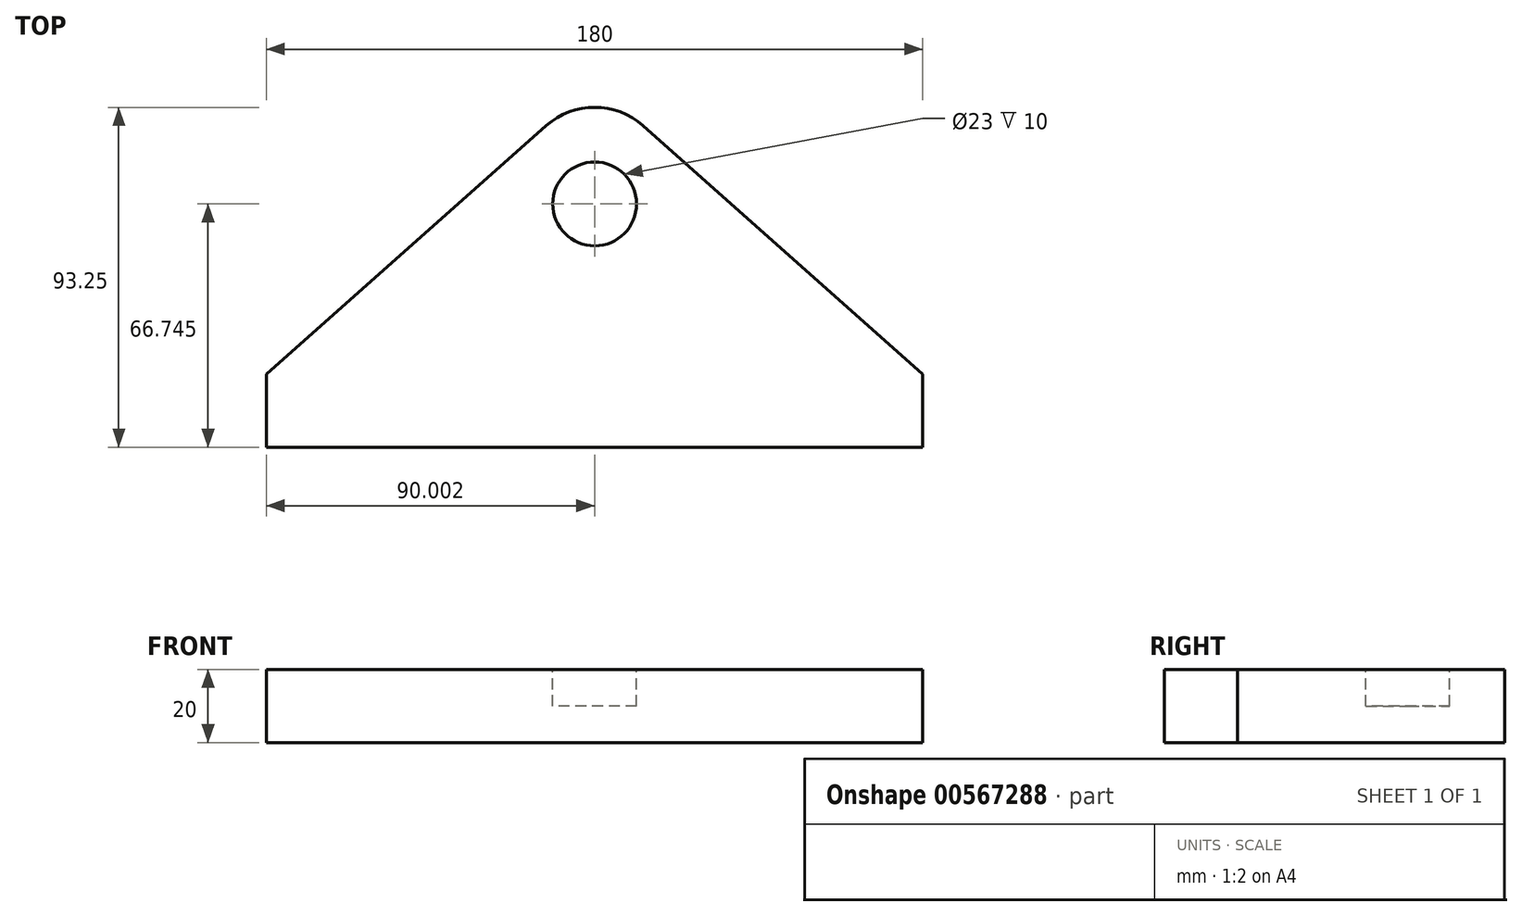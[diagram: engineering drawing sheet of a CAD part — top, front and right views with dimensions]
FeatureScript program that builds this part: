
annotation { "Feature Type Name" : "Feature", "Feature Type Description" : "" }
export const myFeature = defineFeature(function(context is Context, id is Id, definition is map)
    precondition{}
    {
        {
            var Q0;
            Q0=qCreatedBy(makeId("Top.planeOp"),FACE);
            var sketch = newSketch(context, id + "F0", { "sketchPlane" : qUnion([Q0])});
            skLineSegment(sketch, "E0.bottom", {"start": v(-112.55, 59.5) * mm, "end": v(67.45, 59.5) * mm});
            skLineSegment(sketch, "E0.top", {"start": v(-112.55, -40.5) * mm, "end": v(67.45, -40.5) * mm});
            skLineSegment(sketch, "E0.left", {"start": v(-112.55, 59.5) * mm, "end": v(-112.55, -40.5) * mm});
            skLineSegment(sketch, "E0.right", {"start": v(67.45, 59.5) * mm, "end": v(67.45, -40.5) * mm});
            skLineSegment(sketch, "E1", {"start": v(-112.55, -40.5) * mm, "end": v(-112.55, -20.5) * mm});
            skLineSegment(sketch, "E2", {"start": v(67.45, -40.5) * mm, "end": v(67.45, -20.5) * mm});
            skLineSegment(sketch, "E3", {"start": v(-112.55, 59.5) * mm, "end": v(-22.55, 59.5) * mm});
            skLineSegment(sketch, "E4", {"start": v(-112.55, -20.5) * mm, "end": v(-35.84, 47.7) * mm});
            skLineSegment(sketch, "E5", {"start": v(-9.26, 47.7) * mm, "end": v(67.45, -20.5) * mm});
            skPoint(sketch, "E6.visualSharp", {"position": v(-22.55, 59.5) * mm});
            skArc(sketch, "E6.filletArc", {"start": v(-9.26, 47.7) * mm, "mid": v(-22.55, 52.75) * mm, "end": v(-35.84, 47.7) * mm});
            skSolve(sketch);
        }
        {
            var Q0;
            Q0=makeQuery(id+"F0.imprint","IMPRINT",FACE,{"disambiguationData":[TD([[makeQuery(id+"F0.imprint","IMPRINT",EDGE,{"derivedFrom":sQuery(id+"F0.wireOp",EDGE,"E0.top")}),1.0]])]});
            extrude(context, id + "F1", {"entities" : qUnion([Q0]), "depth" : 20 * mm, "offsetDistance" : 25 * mm});
        }
        {
            var Q0;
            Q0=makeQuery(id+"F1.opExtrude","CAP_FACE",FACE,{"disambiguationData":[OSD([sQuery(id+"F0.wireOp",EDGE,"E0.top"),sQuery(id+"F0.wireOp",EDGE,"E1"),sQuery(id+"F0.wireOp",EDGE,"E2"),sQuery(id+"F0.wireOp",EDGE,"E4"),sQuery(id+"F0.wireOp",EDGE,"E5"),sQuery(id+"F0.wireOp",EDGE,"E6.filletArc")])],"isStart":false});
            var sketch = newSketch(context, id + "F2", { "sketchPlane" : qUnion([Q0])});
            skCircle(sketch, "E7", {"center": v(-22.55, 26.25) * mm, "radius": 11.5 * mm});
            skSolve(sketch);
        }
        {
            var Q0;
            Q0=makeQuery(id+"F2.imprint","IMPRINT",FACE,{"disambiguationData":[TD([[makeQuery(id+"F2.imprint","IMPRINT",EDGE,{"derivedFrom":sQuery(id+"F2.wireOp",EDGE,"E7")}),1.0]])]});
            extrude(context, id + "F3", {"entities" : qUnion([Q0]), "operationType" : NewBodyOperationType.REMOVE, "oppositeDirection" : true, "depth" : 10 * mm, "offsetDistance" : 25 * mm});
        }
    });
